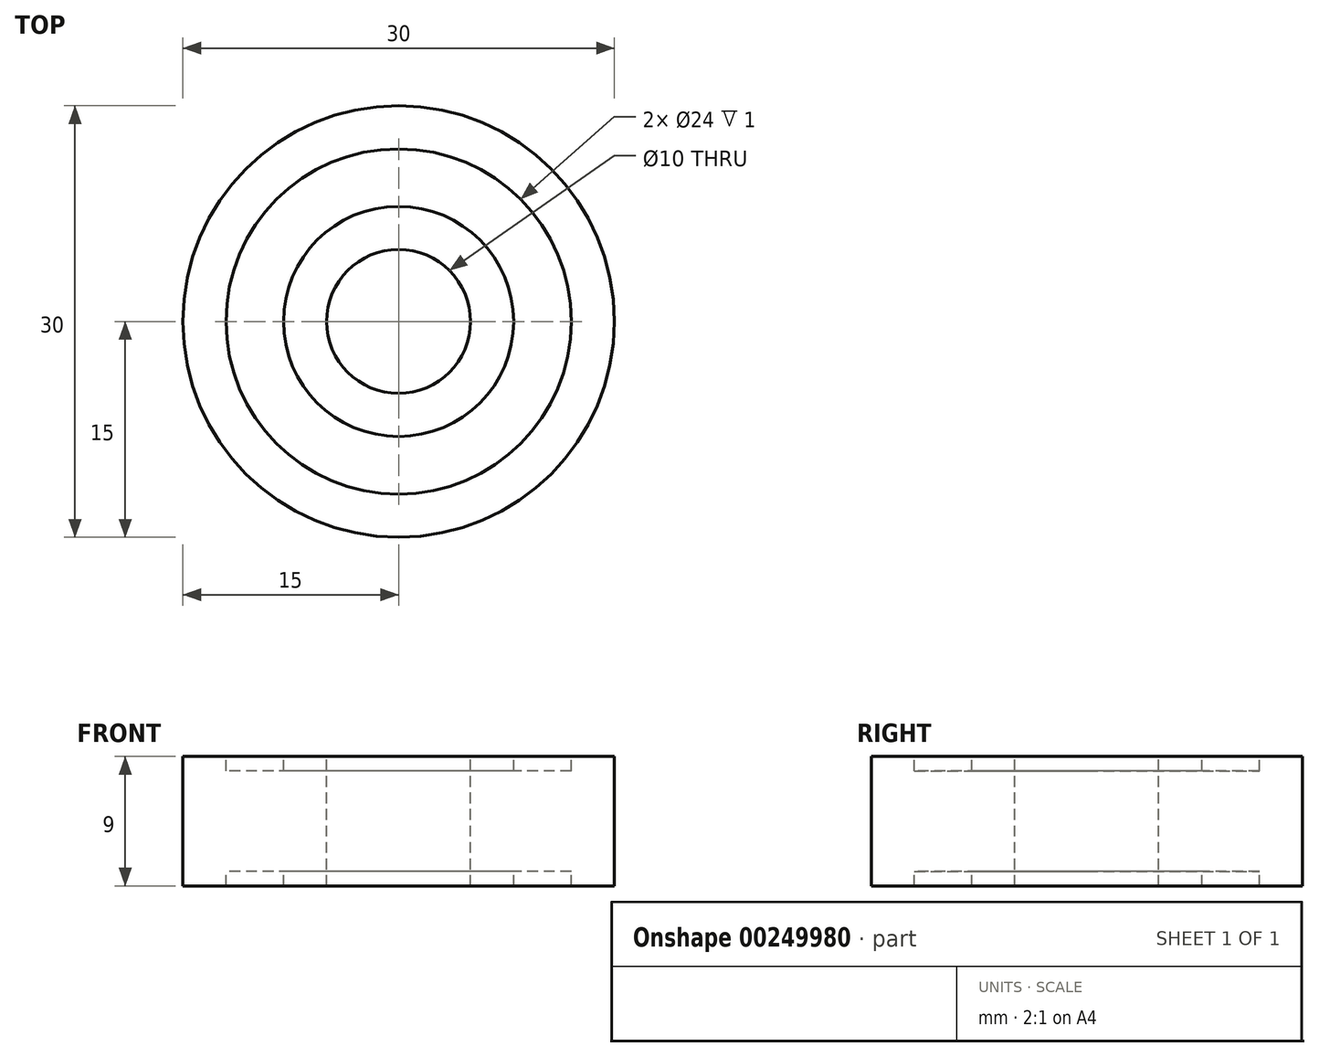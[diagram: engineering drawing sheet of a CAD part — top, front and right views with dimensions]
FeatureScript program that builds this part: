
annotation { "Feature Type Name" : "Feature", "Feature Type Description" : "" }
export const myFeature = defineFeature(function(context is Context, id is Id, definition is map)
    precondition{}
    {
        {
            var Q0;
            Q0=qCreatedBy(makeId("Front.planeOp"),FACE);
            var sketch = newSketch(context, id + "F0", { "sketchPlane" : qUnion([Q0])});
            skLineSegment(sketch, "E0", {"start": v(-15, 4.5) * mm, "end": v(-15, 0) * mm});
            skLineSegment(sketch, "E1", {"start": v(-15, 4.5) * mm, "end": v(-12, 4.5) * mm});
            skLineSegment(sketch, "E2", {"start": v(-5, 4.5) * mm, "end": v(-5, 0) * mm});
            skLineSegment(sketch, "E3", {"start": v(-12, 4.5) * mm, "end": v(-12, 3.5) * mm});
            skLineSegment(sketch, "E4", {"start": v(-8, 4.5) * mm, "end": v(-8, 3.5) * mm});
            skLineSegment(sketch, "E5", {"start": v(-12, 3.5) * mm, "end": v(-8, 3.5) * mm});
            skLineSegment(sketch, "E6.trimOffspring", {"start": v(-8, 4.5) * mm, "end": v(-5, 4.5) * mm});
            skPoint(sketch, "E7", {"position": v(0, 0) * mm});
            skLineSegment(sketch, "E8", {"start": v(0, 16.42) * mm, "end": v(0, -13.94) * mm});
            skLineSegment(sketch, "E9", {"start": v(-20, 0) * mm, "end": v(1.48, 0) * mm, "construction": true});
            skLineSegment(sketch, "E10.MirrorCS", {"start": v(-12, -4.5) * mm, "end": v(-12, -3.5) * mm});
            skLineSegment(sketch, "E11.MirrorCS", {"start": v(-8, -4.5) * mm, "end": v(-8, -3.5) * mm});
            skLineSegment(sketch, "E12.MirrorCS", {"start": v(-8, -4.5) * mm, "end": v(-5, -4.5) * mm});
            skLineSegment(sketch, "E13.MirrorCS", {"start": v(-15, -4.5) * mm, "end": v(-12, -4.5) * mm});
            skLineSegment(sketch, "E14.MirrorCS", {"start": v(-15, -4.5) * mm, "end": v(-15, 0) * mm});
            skLineSegment(sketch, "E15.MirrorCS", {"start": v(-12, -3.5) * mm, "end": v(-8, -3.5) * mm});
            skLineSegment(sketch, "E16.MirrorCS", {"start": v(-5, -4.5) * mm, "end": v(-5, 0) * mm});
            skSolve(sketch);
        }
        {
            var Q0;
            Q0=qSketchRegion(id+"F0",true);
            var Q1;
            Q1=sQuery(id+"F0.wireOp",EDGE,"E8");
            revolve(context, id + "F1", {"entities" : qUnion([Q0]), "axis" : qUnion([Q1]), "revolveType" : RevolveType.FULL});
        }
    });
